# Revit family: NLRS_33_GM_FB_TC_STORAX_vloerluik_BVS-250_BCB
name_source: partatom
category: Generic Models
revit_build: Autodesk Revit 2014 (Build: 20130308_1515(x64)
units: mm (PartAtom-declared; Revit-internal decimal feet)

## types (1)
- NLRS_33_GM_FB_TC_STORAX_vloerluik_BVS-250_BCB
    Default Elevation = 0 mm  [stored 0 ft]
    Manufacturer = Storax
    Model = BV
    URL = http://www.storax.nl
    belasting = 125 kN
    binnenluik = tbv betonvulling
    binnenmaat_breedte = 1000 mm  [stored 3.28084 ft]
    binnenmaat_lengte = 1000 mm  [stored 3.28084 ft]
    brandwerend 90 min = nee
    gasdrukveer = nee
    gewicht = 78
    geïsoleerd = nee
    liggers_lengte = 950 mm  [stored 3.1168 ft]
    materiaal = bcb_staal
    productgroep = Vloerluiken
    rubberen_afdichting = enkel
    scharnierend = nee
    sluiting = 4
    uitwendige_breedte = 1135 mm  [stored 3.72375 ft]
    uitwendige_lengte = 1135 mm  [stored 3.72375 ft]
    vergrendeling = nee
    versterking 106 110 = Yes
    versterking 66 = Yes
    versterking 88 = Yes
    vullen_met_beton = ja

note: [stored X ft] marks values corroborated as IEEE doubles in the binary element streams (Revit-internal decimal feet)

## geometry (parser evidence)
native form markers: Blend x783, Sweep x12
no freeform markers — native parametric forms only
